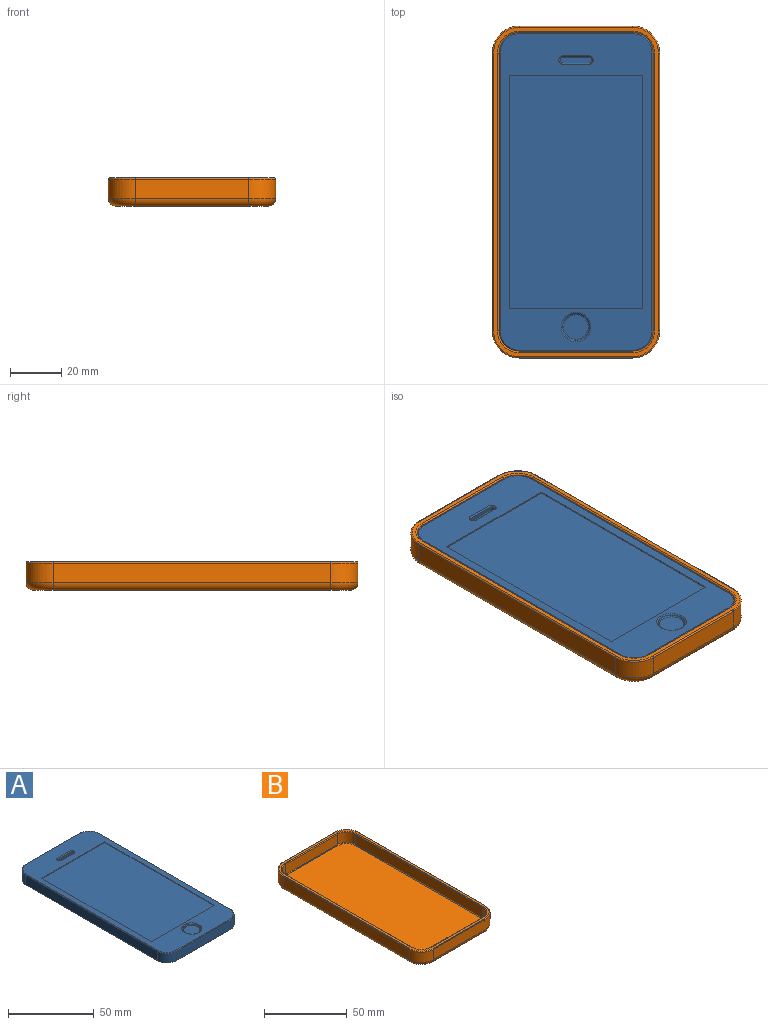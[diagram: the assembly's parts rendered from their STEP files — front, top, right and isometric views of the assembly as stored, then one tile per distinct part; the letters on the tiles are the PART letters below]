
ASSEMBLY  parts=2 mates=1
PART A: 43 faces, bbox 60x124x7.5 mm
  f0: plane 123x59mm, normal (0,0,1), area 2364.3mm2, adj f8,f13,f14,f15,f16,f31,f32,f33
  f1: plane 108x6.5mm, normal (-1,0,0), area 702mm2, adj f9,f12,f30,f38
  f2: plane 44x6.5mm, normal (0,-1,0), area 286mm2, adj f9,f10,f26,f34
  f3: plane 108x6.5mm, normal (1,0,0), area 702mm2, adj f10,f11,f23,f31
  f4: plane 44x6.5mm, normal (0,1,0), area 286mm2, adj f11,f12,f27,f35
  f5: plane 123x59mm, normal (0,0,-1), area 7208.7mm2, adj f23,f24,f25,f26,f27,f28,f29,f30
  f6: plane 9.5x9.5mm, normal (0,0,1), area 70.9mm2, adj f7
  f7: torus R=4.75mm, axis (0,0,1), area 25mm2, adj f6,f8
  f8: torus R=5.75mm, axis (0,0,1), area 26.8mm2, adj f0,f7
  f9: cylinder r=8mm len=8mm, axis (0,0,1), area 81.7mm2, adj f1,f2,f28,f36
  f10: cylinder r=8mm len=8mm, axis (0,0,-1), area 81.7mm2, adj f2,f3,f24,f32
  f11: cylinder r=8mm len=8mm, axis (0,0,1), area 81.7mm2, adj f3,f4,f25,f33
  f12: cylinder r=8mm len=8mm, axis (0,0,-1), area 81.7mm2, adj f1,f4,f29,f37
  f13: plane 52x0.5mm, normal (0,1,0), area 26mm2, adj f0,f14,f16,f17
  f14: plane 90.36x0.5mm, normal (-1,0,0), area 45.2mm2, adj f0,f13,f15,f17
  f15: plane 52x0.5mm, normal (0,-1,0), area 26mm2, adj f0,f14,f16,f17
  f16: plane 90.36x0.5mm, normal (1,0,0), area 45.2mm2, adj f0,f13,f15,f17
  f17: plane 90.36x52mm, normal (0,0,1), area 4698.7mm2, adj f13,f14,f15,f16
  f18: plane 10.08x1.5mm, normal (0,-1,0), area 15.1mm2, adj f19,f21,f22,f39
  f19: cylinder r=1.15mm len=2.3mm, axis (0,0,1), area 5.4mm2, adj f18,f20,f22,f40
  f20: plane 10.08x1.5mm, normal (0,1,0), area 15.1mm2, adj f19,f21,f22,f42
  f21: cylinder r=1.15mm len=2.3mm, axis (0,0,1), area 5.4mm2, adj f18,f20,f22,f41
  f22: plane 12.38x2.3mm, normal (0,0,1), area 27.3mm2, adj f18,f19,f20,f21
  f23: plane 108x0.5mm, normal (0.71,0,-0.71), area 76.4mm2, adj f3,f5,f24,f25
  f24: cone r=7.5mm half-angle=45deg, axis (0,0,1), area 8.6mm2, adj f5,f10,f23,f26
  f25: cone r=7.5mm half-angle=45deg, axis (0,0,1), area 8.6mm2, adj f5,f11,f23,f27
  f26: plane 44x0.5mm, normal (0,-0.71,-0.71), area 31.1mm2, adj f2,f5,f24,f28
  f27: plane 44x0.5mm, normal (0,0.71,-0.71), area 31.1mm2, adj f4,f5,f25,f29
  f28: cone r=7.5mm half-angle=45deg, axis (0,0,1), area 8.6mm2, adj f5,f9,f26,f30
  f29: cone r=7.5mm half-angle=45deg, axis (0,0,1), area 8.6mm2, adj f5,f12,f27,f30
  f30: plane 108x0.5mm, normal (-0.71,0,-0.71), area 76.4mm2, adj f1,f5,f28,f29
  f31: plane 108x0.5mm, normal (0.71,0,0.71), area 76.4mm2, adj f0,f3,f32,f33
  f32: cone r=7.5mm half-angle=45deg, axis (0,0,-1), area 8.6mm2, adj f0,f10,f31,f34
  f33: cone r=7.5mm half-angle=45deg, axis (0,0,-1), area 8.6mm2, adj f0,f11,f31,f35
  f34: plane 44x0.5mm, normal (0,-0.71,0.71), area 31.1mm2, adj f0,f2,f32,f36
  f35: plane 44x0.5mm, normal (0,0.71,0.71), area 31.1mm2, adj f0,f4,f33,f37
  f36: cone r=7.5mm half-angle=45deg, axis (0,0,-1), area 8.6mm2, adj f0,f9,f34,f38
  f37: cone r=7.5mm half-angle=45deg, axis (0,0,-1), area 8.6mm2, adj f0,f12,f35,f38
  f38: plane 108x0.5mm, normal (-0.71,0,0.71), area 76.4mm2, adj f0,f1,f36,f37
  f39: plane 10.08x0.5mm, normal (0,-0.71,0.71), area 7.1mm2, adj f0,f18,f40,f41
  f40: cone r=1.15mm half-angle=45deg, axis (0,0,1), area 3.1mm2, adj f0,f19,f39,f42
  f41: cone r=1.15mm half-angle=45deg, axis (0,0,1), area 3.1mm2, adj f0,f21,f39,f42
  f42: plane 10.08x0.5mm, normal (0,0.71,0.71), area 7.1mm2, adj f0,f20,f40,f41
PART B: 51 faces, bbox 66.7x130.7x11 mm
  f0: plane 128x64mm, normal (0,0,1), area 543.2mm2, adj f27,f28,f29,f30,f31,f32,f33,f34
  f1: plane 108x7.5mm, normal (-1,0,0), area 810mm2, adj f6,f9,f40,f48
  f2: plane 44x7.5mm, normal (0,-1,0), area 330mm2, adj f6,f7,f41,f44
  f3: plane 108x7.5mm, normal (1,0,0), area 810mm2, adj f7,f8,f37,f45
  f4: plane 44x7.5mm, normal (0,1,0), area 330mm2, adj f8,f9,f36,f49
  f5: plane 123x59mm, normal (0,0,-1), area 7208.7mm2, adj f43,f44,f45,f46,f47,f48,f49,f50
  f6: cylinder r=10.5mm len=10.5mm, axis (0,0,1), area 123.7mm2, adj f1,f2,f42,f46
  f7: cylinder r=10.5mm len=10.5mm, axis (0,0,-1), area 123.7mm2, adj f2,f3,f39,f43
  f8: cylinder r=10.5mm len=10.5mm, axis (0,0,1), area 123.7mm2, adj f3,f4,f35,f47
  f9: cylinder r=10.5mm len=10.5mm, axis (0,0,-1), area 123.7mm2, adj f1,f4,f38,f50
  f10: plane 108x7.5mm, normal (1,0,0), area 810mm2, adj f15,f18,f22,f34
  f11: plane 44x7.5mm, normal (0,1,0), area 330mm2, adj f15,f16,f19,f30
  f12: plane 108x7.5mm, normal (-1,0,0), area 810mm2, adj f16,f17,f23,f27
  f13: plane 44x7.5mm, normal (0,-1,0), area 330mm2, adj f17,f18,f26,f31
  f14: plane 123x59mm, normal (0,0,1), area 7208.7mm2, adj f19,f20,f21,f22,f23,f24,f25,f26
  f15: cylinder r=8mm len=8mm, axis (0,0,1), area 94.2mm2, adj f10,f11,f20,f32
  f16: cylinder r=8mm len=8mm, axis (0,0,-1), area 94.2mm2, adj f11,f12,f21,f28
  f17: cylinder r=8mm len=8mm, axis (0,0,1), area 94.2mm2, adj f12,f13,f25,f29
  f18: cylinder r=8mm len=8mm, axis (0,0,-1), area 94.2mm2, adj f10,f13,f24,f33
  f19: cylinder r=0.5mm len=44mm, axis (-1,0,0), area 34.6mm2, adj f11,f14,f20,f21
  f20: torus R=7.5mm, axis (0,0,1), area 9.6mm2, adj f14,f15,f19,f22
  f21: torus R=7.5mm, axis (0,0,1), area 9.6mm2, adj f14,f16,f19,f23
  f22: cylinder r=0.5mm len=108mm, axis (0,1,0), area 84.8mm2, adj f10,f14,f20,f24
  f23: cylinder r=0.5mm len=108mm, axis (0,-1,0), area 84.8mm2, adj f12,f14,f21,f25
  f24: torus R=7.5mm, axis (0,0,1), area 9.6mm2, adj f14,f18,f22,f26
  f25: torus R=7.5mm, axis (0,0,1), area 9.6mm2, adj f14,f17,f23,f26
  f26: cylinder r=0.5mm len=44mm, axis (1,0,0), area 34.6mm2, adj f13,f14,f24,f25
  f27: cylinder r=0.5mm len=108mm, axis (0,1,0), area 84.8mm2, adj f0,f12,f28,f29
  f28: torus R=8.5mm, axis (0,0,1), area 10.1mm2, adj f0,f16,f27,f30
  f29: torus R=8.5mm, axis (0,0,1), area 10.1mm2, adj f0,f17,f27,f31
  f30: cylinder r=0.5mm len=44mm, axis (1,0,0), area 34.6mm2, adj f0,f11,f28,f32
  f31: cylinder r=0.5mm len=44mm, axis (-1,0,0), area 34.6mm2, adj f0,f13,f29,f33
  f32: torus R=8.5mm, axis (0,0,1), area 10.1mm2, adj f0,f15,f30,f34
  f33: torus R=8.5mm, axis (0,0,1), area 10.1mm2, adj f0,f18,f31,f34
  f34: cylinder r=0.5mm len=108mm, axis (0,-1,0), area 84.8mm2, adj f0,f10,f32,f33
  f35: torus R=10mm, axis (0,0,1), area 12.7mm2, adj f0,f8,f36,f37
  f36: cylinder r=0.5mm len=44mm, axis (1,0,0), area 34.6mm2, adj f0,f4,f35,f38
  f37: cylinder r=0.5mm len=108mm, axis (0,-1,0), area 84.8mm2, adj f0,f3,f35,f39
  f38: torus R=10mm, axis (0,0,1), area 12.7mm2, adj f0,f9,f36,f40
  f39: torus R=10mm, axis (0,0,1), area 12.7mm2, adj f0,f7,f37,f41
  f40: cylinder r=0.5mm len=108mm, axis (0,1,0), area 84.8mm2, adj f0,f1,f38,f42
  f41: cylinder r=0.5mm len=44mm, axis (-1,0,0), area 34.6mm2, adj f0,f2,f39,f42
  f42: torus R=10mm, axis (0,0,1), area 12.7mm2, adj f0,f6,f40,f41
  f43: torus R=7.5mm, axis (0,0,1), area 69.7mm2, adj f5,f7,f44,f45
  f44: cylinder r=3mm len=44mm, axis (1,0,0), area 207.3mm2, adj f2,f5,f43,f46
  f45: cylinder r=3mm len=108mm, axis (0,1,0), area 508.9mm2, adj f3,f5,f43,f47
  f46: torus R=7.5mm, axis (0,0,1), area 69.7mm2, adj f5,f6,f44,f48
  f47: torus R=7.5mm, axis (0,0,1), area 69.7mm2, adj f5,f8,f45,f49
  f48: cylinder r=3mm len=108mm, axis (0,-1,0), area 508.9mm2, adj f1,f5,f46,f50
  f49: cylinder r=3mm len=44mm, axis (-1,0,0), area 207.3mm2, adj f4,f5,f47,f50
  f50: torus R=7.5mm, axis (0,0,1), area 69.7mm2, adj f5,f9,f48,f49
PLACE A t=(3.25,-1.34,-15.58)mm
PLACE B t=(3.25,-1.34,-16.08)mm
MATE fastened A.f3 <-> B.f12  axis (1,0,0) through (33.25,-1.34,-11.83)mm
